# Revit family: Accessory-Step_Can-KOHLER-K-23826_1
name_source: partatom
category: Specialty Equipment
revit_build: Autodesk Revit 2017 (Build: 20160225_1515(x64)
units: mm (PartAtom-declared; Revit-internal decimal feet)

## family parameters
Cut with Voids When Loaded = No
Host = Face
OmniClass Number = 23.31.25.00
OmniClass Title = Toilet and Bath Specialties
Part Type = Normal
Room Calculation Point = No
Round Connector Dimension = Use Diameter
Shared = No

## types (3) — shared parameters
ADA Compliant = No
Assembly Code = C1030200
Date Modified = 10/5/2021
Default Elevation = 0"
Description = Ellongated 13-gallon Step Can
Height = 26 3/8"
Length = 18 13/16"
Manufacturer = KOHLER Co.
Master Format 2014 = 10 28 00
Master Format 2014 Name = Toilet, Bath, and Laundry Accessories
Material = Stainless Steel
Product Documentation Link = https://www.us.kohler.com
Product Page URL = http://www.us.kohler.com
URL = https://www.us.kohler.com
WaterSense Certified = No
Width = 11 1/16"

## per-type parameters (varying)
| type | Finish | Model | Secondary Finish | Type |
| ST-Stainless Steel | KOHLER-Metal-ST-Stainless_Steel | K-23826-ST | Kohler-Plastic-7-Black_Black | 1 |
| STW-Stainless and White | KOHLER-Metal-STW-White_and_Stainless_Steel | K-23826-STW | Kohler-Plastic-0-White | 2 |
| BST-Black Stainless | KOHLER-Metal-BST-Black_Stainless | K-23826-BST | Kohler-Plastic-7-Black_Black | 3 |

## geometry (parser evidence)
native form markers: Sweep x5
no freeform markers — native parametric forms only
